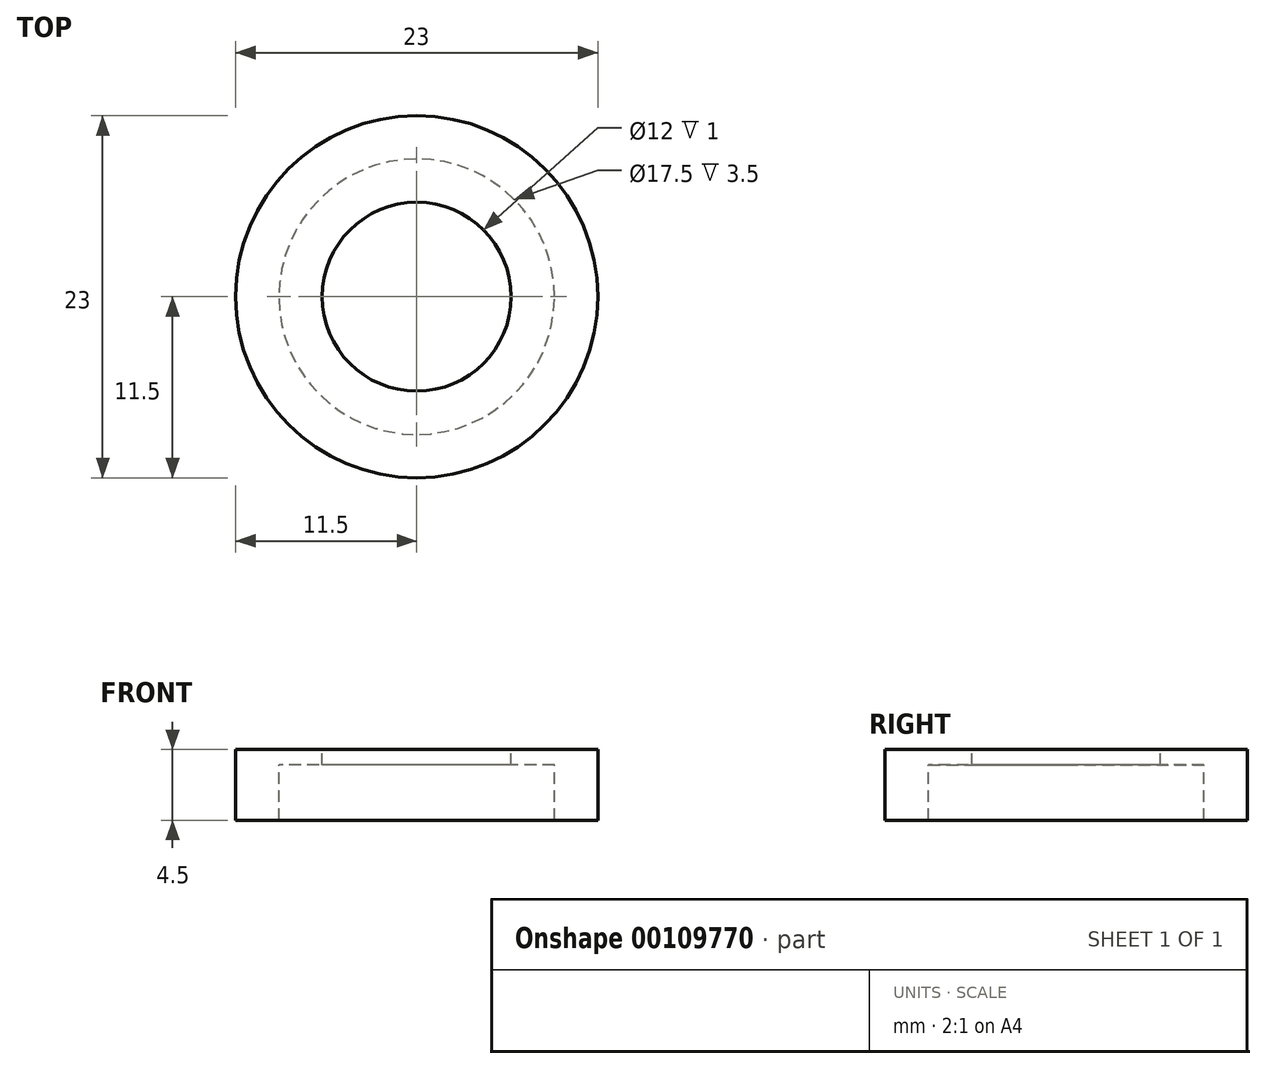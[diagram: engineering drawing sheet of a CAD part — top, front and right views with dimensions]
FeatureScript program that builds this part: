
annotation { "Feature Type Name" : "Feature", "Feature Type Description" : "" }
export const myFeature = defineFeature(function(context is Context, id is Id, definition is map)
    precondition{}
    {
        {
            var Q0;
            Q0=qCreatedBy(makeId("Top.planeOp"),FACE);
            var sketch = newSketch(context, id + "F0", { "sketchPlane" : qUnion([Q0])});
            skCircle(sketch, "E0", {"center": v(0, 0) * mm, "radius": 11.5 * mm});
            skCircle(sketch, "E1", {"center": v(0, 0) * mm, "radius": 8.75 * mm});
            skCircle(sketch, "E2", {"center": v(0, 0) * mm, "radius": 6 * mm});
            skSolve(sketch);
        }
        {
            var Q0;
            Q0=makeQuery(id+"F0.imprint","IMPRINT",FACE,{"disambiguationData":[TD([[makeQuery(id+"F0.imprint","IMPRINT",EDGE,{"derivedFrom":sQuery(id+"F0.wireOp",EDGE,"E1")}),1.0]])]});
            extrude(context, id + "F1", {"entities" : qUnion([Q0]), "oppositeDirection" : true, "depth" : 1 * mm});
        }
        {
            var Q0;
            Q0 = qSketchRegion(id + "F0", true);
            extrude(context, id + "F2", {"entities" : qUnion([Q0]), "operationType" : NewBodyOperationType.ADD, "oppositeDirection" : true, "depth" : 4.5 * mm});
        }
    });
